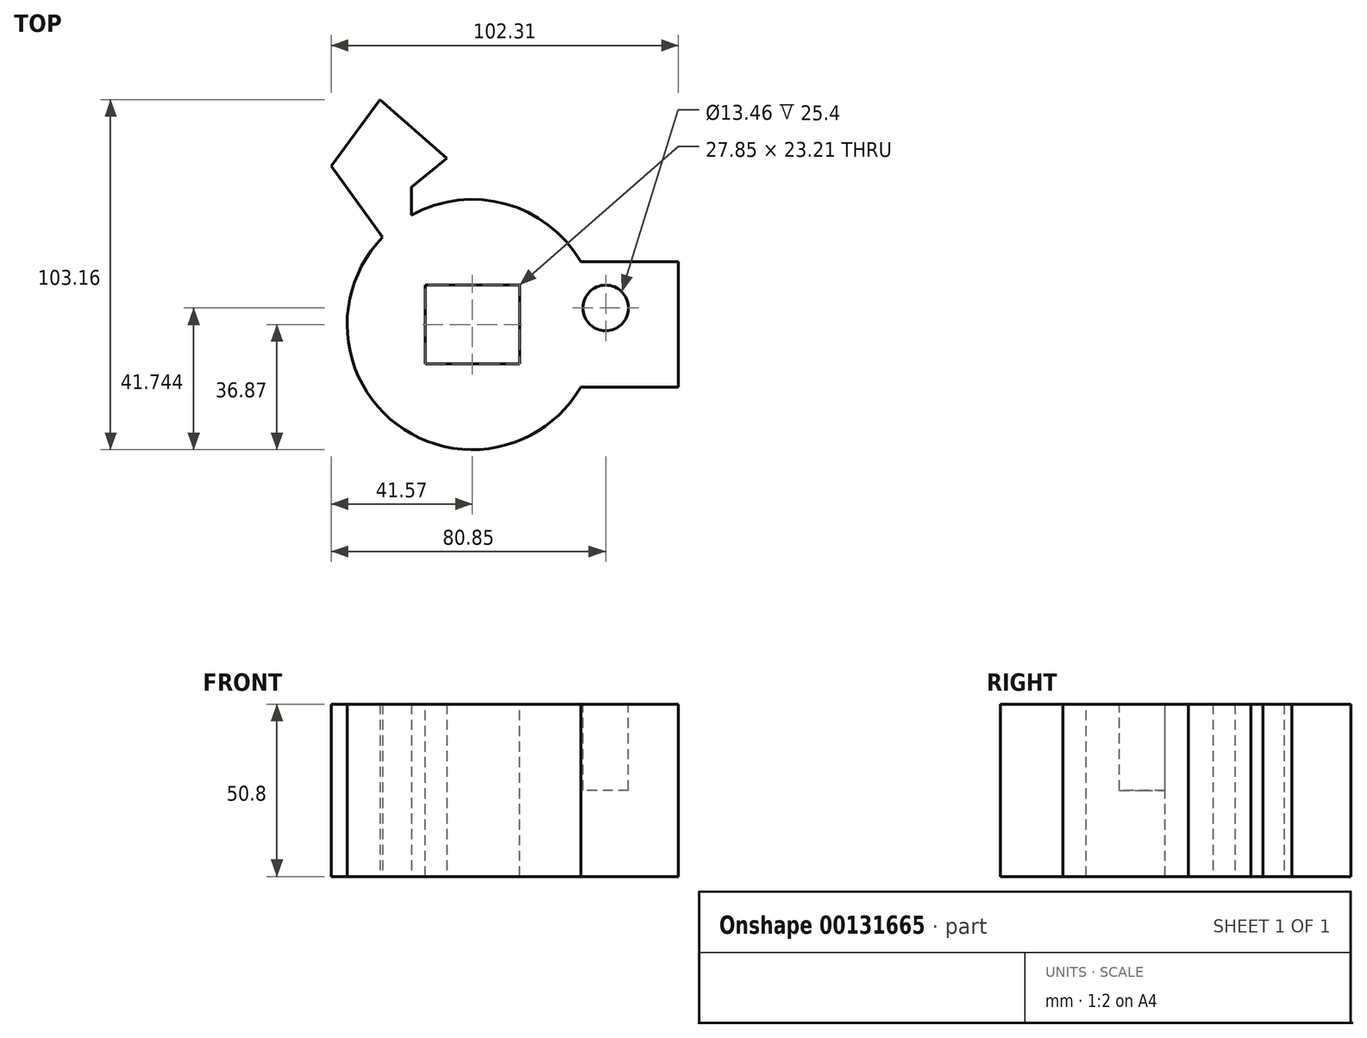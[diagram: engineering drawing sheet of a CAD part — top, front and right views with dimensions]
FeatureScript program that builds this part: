
annotation { "Feature Type Name" : "Feature", "Feature Type Description" : "" }
export const myFeature = defineFeature(function(context is Context, id is Id, definition is map)
    precondition{}
    {
        {
            var Q0;
            Q0=qCreatedBy(makeId("Top.planeOp"),FACE);
            var sketch = newSketch(context, id + "F0", { "sketchPlane" : qUnion([Q0])});
            skArc(sketch, "E0", {"start": v(-26.45, 25.7) * mm, "mid": v(-22.25, -29.4) * mm, "end": v(31.92, -18.46) * mm});
            skLineSegment(sketch, "E1", {"start": v(-26.45, 25.7) * mm, "end": v(-41.57, 46.71) * mm});
            skLineSegment(sketch, "E2", {"start": v(-41.57, 46.71) * mm, "end": v(-27.24, 66.29) * mm});
            skLineSegment(sketch, "E3", {"start": v(-27.24, 66.29) * mm, "end": v(-7.47, 48.93) * mm});
            skLineSegment(sketch, "E4", {"start": v(-7.47, 48.93) * mm, "end": v(-17.96, 40.46) * mm});
            skLineSegment(sketch, "E5", {"start": v(-17.96, 40.46) * mm, "end": v(-17.96, 32.2) * mm});
            skLineSegment(sketch, "E6.bottom", {"start": v(60.74, 18.46) * mm, "end": v(31.92, 18.46) * mm});
            skLineSegment(sketch, "E6.top", {"start": v(60.74, -18.46) * mm, "end": v(31.92, -18.46) * mm});
            skLineSegment(sketch, "E6.left", {"start": v(60.74, 18.46) * mm, "end": v(60.74, -18.46) * mm});
            skPoint(sketch, "E6.middle", {"position": v(36.87, 0) * mm});
            skPoint(sketch, "E6.right.start.orphan", {"position": v(13, 18.46) * mm});
            skPoint(sketch, "E7.orphan", {"position": v(13, -18.46) * mm});
            skArc(sketch, "E8.trimOffspring", {"start": v(31.92, 18.46) * mm, "mid": v(9.8, 35.55) * mm, "end": v(-17.96, 32.2) * mm});
            skSolve(sketch);
        }
        {
            var Q0;
            Q0 = qSketchRegion(id + "F0", true);
            extrude(context, id + "F1", {"entities" : qUnion([Q0]), "depth" : 50.8 * mm});
        }
        {
            var Q0;
            Q0=makeQuery(id+"F1.opExtrude","CAP_FACE",FACE,{"disambiguationData":[OSD([sQuery(id+"F0.wireOp",EDGE,"E0"),sQuery(id+"F0.wireOp",EDGE,"E1"),sQuery(id+"F0.wireOp",EDGE,"E2"),sQuery(id+"F0.wireOp",EDGE,"E3"),sQuery(id+"F0.wireOp",EDGE,"E4"),sQuery(id+"F0.wireOp",EDGE,"E5"),sQuery(id+"F0.wireOp",EDGE,"E6.bottom"),sQuery(id+"F0.wireOp",EDGE,"E6.top"),sQuery(id+"F0.wireOp",EDGE,"E6.left"),sQuery(id+"F0.wireOp",EDGE,"E8.trimOffspring")])],"isStart":false});
            var sketch = newSketch(context, id + "F2", { "sketchPlane" : qUnion([Q0])});
            skLineSegment(sketch, "E9.bottom", {"start": v(13.92, 11.6) * mm, "end": v(-13.92, 11.6) * mm});
            skLineSegment(sketch, "E9.top", {"start": v(13.92, -11.6) * mm, "end": v(-13.92, -11.6) * mm});
            skLineSegment(sketch, "E9.left", {"start": v(13.92, 11.6) * mm, "end": v(13.92, -11.6) * mm});
            skLineSegment(sketch, "E9.right", {"start": v(-13.92, 11.6) * mm, "end": v(-13.92, -11.6) * mm});
            skPoint(sketch, "E9.middle", {"position": v(0, 0) * mm});
            skSolve(sketch);
        }
        {
            var Q0;
            Q0 = qSketchRegion(id + "F2", true);
            extrude(context, id + "F3", {"entities" : qUnion([Q0]), "operationType" : NewBodyOperationType.REMOVE, "oppositeDirection" : true, "depth" : 118.99 * mm});
        }
        {
            var Q0;
            Q0=makeQuery(id+"F1.opExtrude","CAP_FACE",FACE,{"disambiguationData":[OSD([sQuery(id+"F0.wireOp",EDGE,"E0"),sQuery(id+"F0.wireOp",EDGE,"E1"),sQuery(id+"F0.wireOp",EDGE,"E2"),sQuery(id+"F0.wireOp",EDGE,"E3"),sQuery(id+"F0.wireOp",EDGE,"E4"),sQuery(id+"F0.wireOp",EDGE,"E5"),sQuery(id+"F0.wireOp",EDGE,"E6.bottom"),sQuery(id+"F0.wireOp",EDGE,"E6.top"),sQuery(id+"F0.wireOp",EDGE,"E6.left"),sQuery(id+"F0.wireOp",EDGE,"E8.trimOffspring")])],"isStart":false});
            var sketch = newSketch(context, id + "F4", { "sketchPlane" : qUnion([Q0])});
            skCircle(sketch, "E10", {"center": v(39.28, 4.87) * mm, "radius": 6.73 * mm});
            skSolve(sketch);
        }
        {
            var Q0;
            Q0 = qSketchRegion(id + "F4", true);
            extrude(context, id + "F5", {"entities" : qUnion([Q0]), "operationType" : NewBodyOperationType.REMOVE, "oppositeDirection" : true, "depth" : 25.4 * mm});
        }
    });
